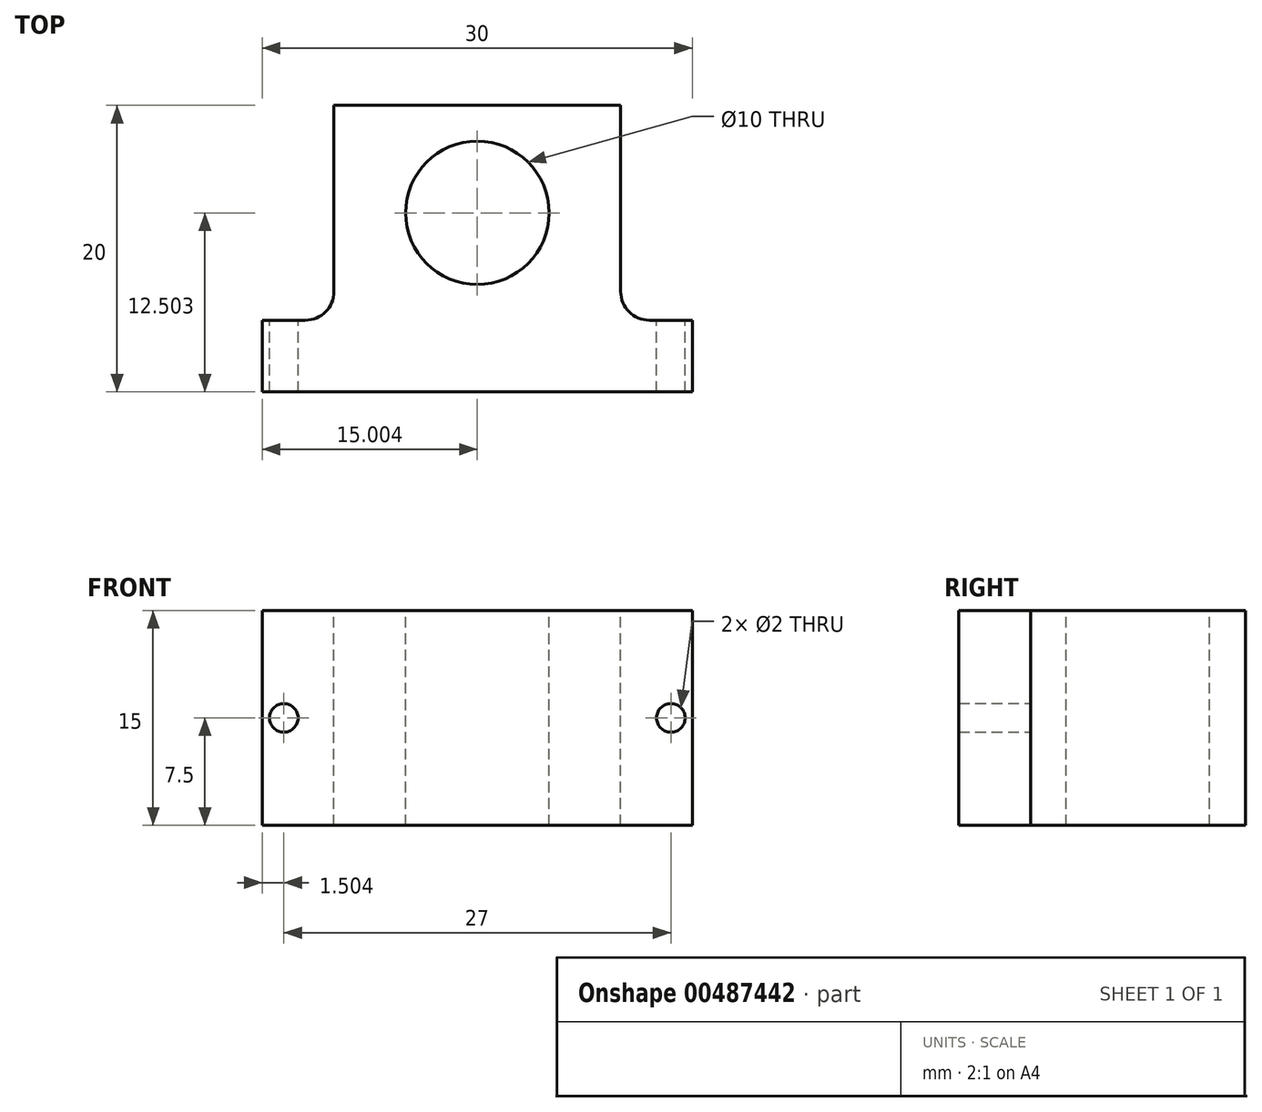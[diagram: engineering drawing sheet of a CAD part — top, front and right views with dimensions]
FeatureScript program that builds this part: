
annotation { "Feature Type Name" : "Feature", "Feature Type Description" : "" }
export const myFeature = defineFeature(function(context is Context, id is Id, definition is map)
    precondition{}
    {
        {
            var Q0;
            Q0=qCreatedBy(makeId("Top.planeOp"),FACE);
            var sketch = newSketch(context, id + "F0", { "sketchPlane" : qUnion([Q0])});
            skLineSegment(sketch, "E0.bottom", {"start": v(-11.83, 14.41) * mm, "end": v(18.17, 14.41) * mm});
            skLineSegment(sketch, "E0.top", {"start": v(-11.83, -5.59) * mm, "end": v(18.17, -5.59) * mm});
            skLineSegment(sketch, "E0.left", {"start": v(-11.83, 14.41) * mm, "end": v(-11.83, -5.59) * mm});
            skLineSegment(sketch, "E0.right", {"start": v(18.17, 14.41) * mm, "end": v(18.17, -5.59) * mm});
            skSolve(sketch);
        }
        {
            var Q0;
            Q0=makeQuery(id+"F0.imprint","IMPRINT",FACE,{"disambiguationData":[TD([[makeQuery(id+"F0.imprint","IMPRINT",EDGE,{"derivedFrom":sQuery(id+"F0.wireOp",EDGE,"E0.bottom")}),-1.0]])]});
            extrude(context, id + "F1", {"entities" : qUnion([Q0]), "depth" : 15 * mm});
        }
        {
            var Q0;
            Q0=makeQuery(id+"F1.opExtrude","CAP_FACE",FACE,{"disambiguationData":[OSD([sQuery(id+"F0.wireOp",EDGE,"E0.bottom"),sQuery(id+"F0.wireOp",EDGE,"E0.top"),sQuery(id+"F0.wireOp",EDGE,"E0.left"),sQuery(id+"F0.wireOp",EDGE,"E0.right")])],"isStart":false});
            var sketch = newSketch(context, id + "F2", { "sketchPlane" : qUnion([Q0])});
            skLineSegment(sketch, "E1", {"start": v(18.17, -5.59) * mm, "end": v(13.17, -5.59) * mm});
            skLineSegment(sketch, "E2", {"start": v(13.17, -5.59) * mm, "end": v(13.17, 14.41) * mm});
            skLineSegment(sketch, "E3", {"start": v(18.17, -5.59) * mm, "end": v(18.17, -0.59) * mm});
            skLineSegment(sketch, "E4", {"start": v(18.17, -0.59) * mm, "end": v(13.17, -0.59) * mm});
            skSolve(sketch);
        }
        {
            var Q0;
            {var subQ3=sQuery(id+"F2.wireOp",EDGE,"E4");Q0=makeQuery(id+"F2.imprint","IMPRINT",FACE,{"disambiguationData":[TD([[makeQuery(id+"F2.imprint","IMPRINT",EDGE,{"derivedFrom":subQ3}),-1.0]])]});}
            extrude(context, id + "F3", {"entities" : qUnion([Q0]), "operationType" : NewBodyOperationType.REMOVE, "oppositeDirection" : true, "depth" : 25 * mm});
        }
        {
            var Q0;
            Q0=makeQuery(id+"F1.opExtrude","CAP_FACE",FACE,{"disambiguationData":[OSD([sQuery(id+"F0.wireOp",EDGE,"E0.bottom"),sQuery(id+"F0.wireOp",EDGE,"E0.top"),sQuery(id+"F0.wireOp",EDGE,"E0.left"),sQuery(id+"F0.wireOp",EDGE,"E0.right")])],"isStart":false});
            var sketch = newSketch(context, id + "F4", { "sketchPlane" : qUnion([Q0])});
            skLineSegment(sketch, "E5", {"start": v(-11.83, -5.59) * mm, "end": v(-6.83, -5.59) * mm});
            skLineSegment(sketch, "E6", {"start": v(-11.83, -5.59) * mm, "end": v(-11.83, -0.59) * mm});
            skLineSegment(sketch, "E7", {"start": v(-6.83, -5.59) * mm, "end": v(-6.83, -0.59) * mm});
            skLineSegment(sketch, "E8", {"start": v(-6.83, -0.59) * mm, "end": v(-11.83, -0.59) * mm});
            skLineSegment(sketch, "E9", {"start": v(-6.83, -0.59) * mm, "end": v(-6.83, 14.41) * mm});
            skSolve(sketch);
        }
        {
            var Q0;
            {var subQ0=sQuery(id+"F4.wireOp",EDGE,"E8");Q0=makeQuery(id+"F4.imprint","IMPRINT",FACE,{"disambiguationData":[TD([[makeQuery(id+"F4.imprint","IMPRINT",EDGE,{"derivedFrom":subQ0}),-1.0]])]});}
            extrude(context, id + "F5", {"entities" : qUnion([Q0]), "operationType" : NewBodyOperationType.REMOVE, "oppositeDirection" : true, "depth" : 25 * mm});
        }
        {
            var Q0;
            Q0=makeQuery(id+"F1.opExtrude","CAP_FACE",FACE,{"disambiguationData":[OSD([sQuery(id+"F0.wireOp",EDGE,"E0.bottom"),sQuery(id+"F0.wireOp",EDGE,"E0.top"),sQuery(id+"F0.wireOp",EDGE,"E0.left"),sQuery(id+"F0.wireOp",EDGE,"E0.right")])],"isStart":false});
            var sketch = newSketch(context, id + "F6", { "sketchPlane" : qUnion([Q0])});
            skLineSegment(sketch, "E10", {"start": v(-6.83, -0.59) * mm, "end": v(13.17, -0.59) * mm});
            skCircle(sketch, "E11", {"center": v(3.17, 6.91) * mm, "radius": 5 * mm});
            skPoint(sketch, "E11.centerSnap0", {"position": v(-6.83, 6.91) * mm});
            skPoint(sketch, "E11.centerSnap1", {"position": v(3.17, 14.41) * mm});
            skSolve(sketch);
        }
        {
            var Q0;
            Q0=makeQuery(id+"F6.imprint","IMPRINT",FACE,{"disambiguationData":[TD([[makeQuery(id+"F6.imprint","IMPRINT",EDGE,{"derivedFrom":sQuery(id+"F6.wireOp",EDGE,"E11")}),1.0]])]});
            extrude(context, id + "F7", {"entities" : qUnion([Q0]), "operationType" : NewBodyOperationType.REMOVE, "endBound" : BoundingType.THROUGH_ALL, "oppositeDirection" : true, "depth" : 25 * mm});
        }
        {
            var Q0;
            Q0=makeQuery(id+"F5.boolean.opBoolean","COPY",EDGE,{"derivedFrom":makeQuery(id+"F5.opExtrude","SWEPT_EDGE",EDGE,{"disambiguationData":[OSD([sQuery(id+"F4.wireOp",EDGE,"E7"),sQuery(id+"F4.wireOp",EDGE,"E8"),sQuery(id+"F4.wireOp",EDGE,"E9")])]})});
            var Q1;
            Q1=makeQuery(id+"F3.boolean.opBoolean","COPY",EDGE,{"derivedFrom":makeQuery(id+"F3.opExtrude","SWEPT_EDGE",EDGE,{"disambiguationData":[OSD([sQuery(id+"F2.wireOp",EDGE,"E2"),sQuery(id+"F2.wireOp",EDGE,"E4")])]})});
            fillet(context, id + "F8", {"entities" : qUnion([Q0, Q1]), "radius" : 2 * mm, "tangentPropagation" : true, "allowEdgeOverflow" : false});
        }
        {
            var Q0;
            Q0=makeQuery(id+"F3.boolean.opBoolean","COPY",FACE,{"derivedFrom":makeQuery(id+"F3.opExtrude","SWEPT_FACE",FACE,{"disambiguationData":[OSD([sQuery(id+"F2.wireOp",EDGE,"E4")])]})});
            var sketch = newSketch(context, id + "F9", { "sketchPlane" : qUnion([Q0])});
            skCircle(sketch, "E12", {"center": v(-16.67, 7.5) * mm, "radius": 1 * mm});
            skPoint(sketch, "E12.centerSnap0", {"position": v(-16.67, 15) * mm});
            skPoint(sketch, "E12.centerSnap1", {"position": v(-15.17, 7.5) * mm});
            skSolve(sketch);
        }
        {
            var Q0;
            Q0=makeQuery(id+"F5.boolean.opBoolean","COPY",FACE,{"derivedFrom":makeQuery(id+"F5.opExtrude","SWEPT_FACE",FACE,{"disambiguationData":[OSD([sQuery(id+"F4.wireOp",EDGE,"E8")])]})});
            var sketch = newSketch(context, id + "F10", { "sketchPlane" : qUnion([Q0])});
            skCircle(sketch, "E13", {"center": v(10.33, 7.5) * mm, "radius": 1 * mm});
            skPoint(sketch, "E13.centerSnap0", {"position": v(10.33, 0) * mm});
            skPoint(sketch, "E13.centerSnap1", {"position": v(8.83, 7.5) * mm});
            skSolve(sketch);
        }
        {
            var Q0;
            Q0=makeQuery(id+"F10.imprint","IMPRINT",FACE,{"disambiguationData":[TD([[makeQuery(id+"F10.imprint","IMPRINT",EDGE,{"derivedFrom":sQuery(id+"F10.wireOp",EDGE,"E13")}),1.0]])]});
            extrude(context, id + "F11", {"entities" : qUnion([Q0]), "operationType" : NewBodyOperationType.REMOVE, "oppositeDirection" : true, "depth" : 25 * mm});
        }
        {
            var Q0;
            Q0=makeQuery(id+"F9.imprint","IMPRINT",FACE,{"disambiguationData":[TD([[makeQuery(id+"F9.imprint","IMPRINT",EDGE,{"derivedFrom":sQuery(id+"F9.wireOp",EDGE,"E12")}),1.0]])]});
            extrude(context, id + "F12", {"entities" : qUnion([Q0]), "operationType" : NewBodyOperationType.REMOVE, "endBound" : BoundingType.THROUGH_ALL, "oppositeDirection" : true, "depth" : 25 * mm});
        }
    });
